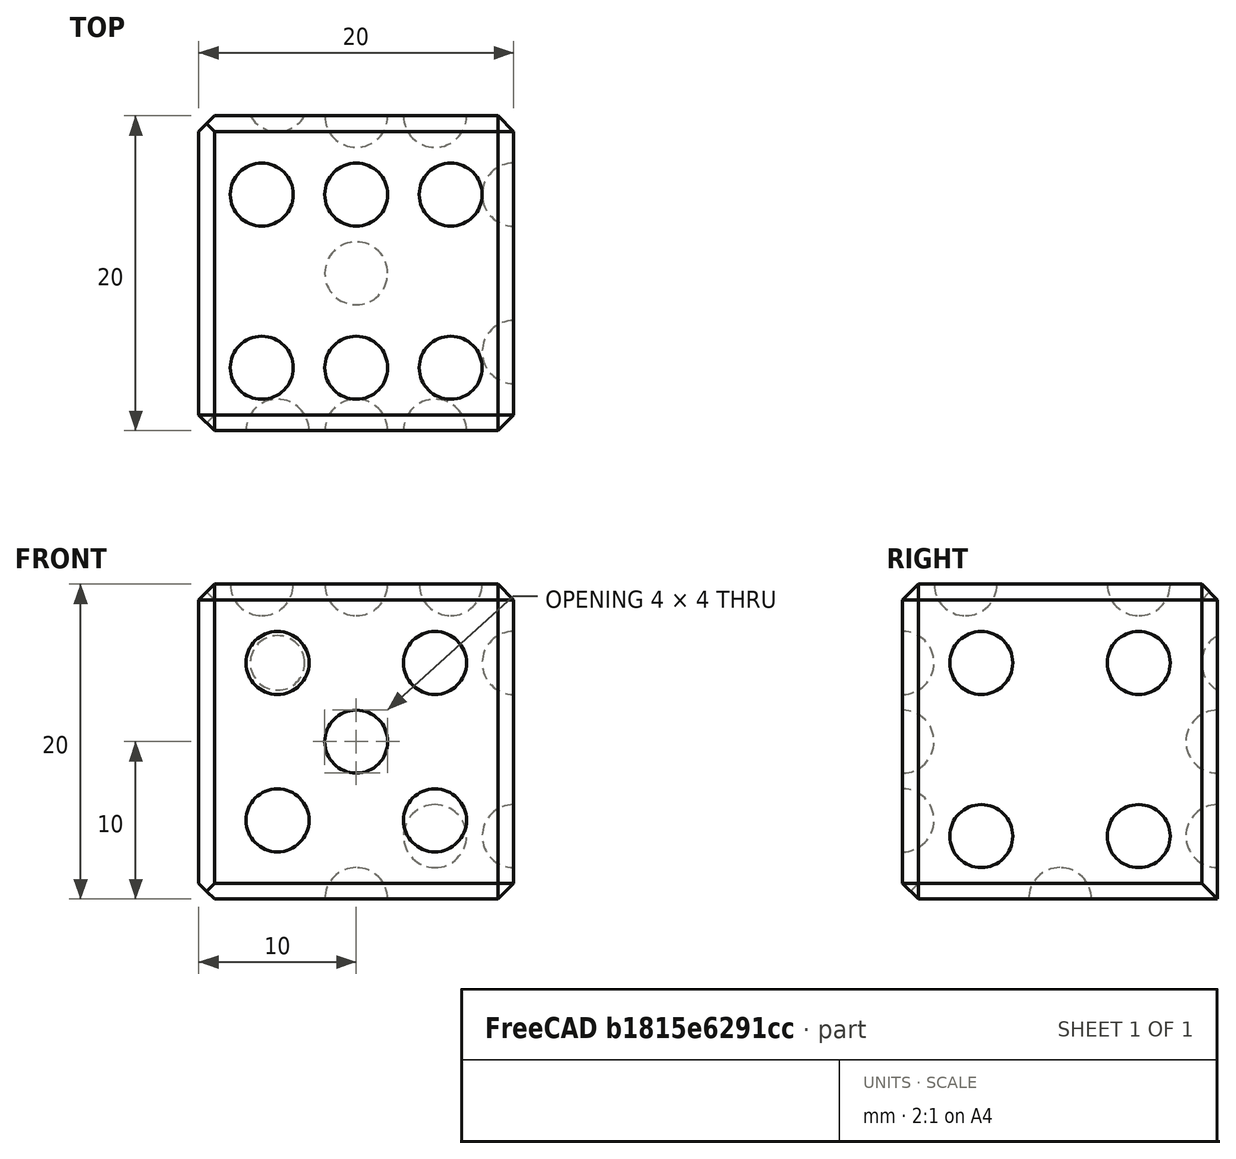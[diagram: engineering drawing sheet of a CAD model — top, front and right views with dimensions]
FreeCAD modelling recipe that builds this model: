
FCSTD DOCUMENT  (FreeCAD 0.21R33694 (Git))
Label: OJT1_T013R012_DAU
License: All rights reserved
LicenseURL: http://en.wikipedia.org/wiki/All_rights_reserved
objects: Part::Sphere×21, Part::MultiFuse×7, Part::Cut×6, Part::Chamfer×3, Part::Box×1
note: 38 computed .brp shape members not serialized (recipe doc carries the construction recipe); baked Part::Feature solids carry a one-line shape summary decoded from their .brp

FEATURE [Part::Box] Box  label="DAU"
  AttacherType = Attacher::AttachEngine3D
  Height = 20
  Length = 20
  Width = 20
FEATURE [Part::Sphere] Sphere
  Angle1 = -90
  Angle2 = 90
  Angle3 = 360
  AttacherType = Attacher::AttachEngine3D
  Placement = pos=(4,4,20) rot=(0,0,1;0rad)
  Radius = 2
FEATURE [Part::Chamfer] Chamfer
  Base = -> Box
  Edges = 9 edges r=1: [Edge1,Edge2,Edge5,Edge6,Edge7,Edge8,Edge9,Edge10,Edge12]
FEATURE [Part::Chamfer] Chamfer001
  Base = -> Chamfer
  Edges = 1 edges r=1: [Edge1]
FEATURE [Part::Chamfer] Chamfer002
  Base = -> Chamfer001
  Edges = 1 edges r=1: [Edge3]
FEATURE [Part::Sphere] Sphere001
  Angle1 = -90
  Angle2 = 90
  Angle3 = 360
  AttacherType = Attacher::AttachEngine3D
  Placement = pos=(10,4,20) rot=(0,0,1;0rad)
  Radius = 2
FEATURE [Part::Sphere] Sphere002
  Angle1 = -90
  Angle2 = 90
  Angle3 = 360
  AttacherType = Attacher::AttachEngine3D
  Placement = pos=(16,4,20) rot=(0,0,1;0rad)
  Radius = 2
FEATURE [Part::MultiFuse] Fusion
  Refine = true
  Shapes = -> [Sphere,Sphere001,Sphere002]
FEATURE [Part::Sphere] Sphere003
  Angle1 = -90
  Angle2 = 90
  Angle3 = 360
  AttacherType = Attacher::AttachEngine3D
  Placement = pos=(4,4,20) rot=(0,0,1;0rad)
  Radius = 2
FEATURE [Part::Sphere] Sphere004
  Angle1 = -90
  Angle2 = 90
  Angle3 = 360
  AttacherType = Attacher::AttachEngine3D
  Placement = pos=(10,4,20) rot=(0,0,1;0rad)
  Radius = 2
FEATURE [Part::Sphere] Sphere005
  Angle1 = -90
  Angle2 = 90
  Angle3 = 360
  AttacherType = Attacher::AttachEngine3D
  Placement = pos=(16,4,20) rot=(0,0,1;0rad)
  Radius = 2
FEATURE [Part::MultiFuse] Fusion001
  Placement = pos=(0,11,0) rot=(0,0,1;0rad)
  Refine = true
  Shapes = -> [Sphere003,Sphere004,Sphere005]
FEATURE [Part::MultiFuse] Fusion002
  Refine = true
  Shapes = -> [Fusion001,Fusion]
FEATURE [Part::Sphere] Sphere006
  Angle1 = -90
  Angle2 = 90
  Angle3 = 360
  AttacherType = Attacher::AttachEngine3D
  Placement = pos=(10,0,10) rot=(0,0,1;0rad)
  Radius = 2
FEATURE [Part::Sphere] Sphere007
  Angle1 = -90
  Angle2 = 90
  Angle3 = 360
  AttacherType = Attacher::AttachEngine3D
  Placement = pos=(15,0,15) rot=(0,0,1;0rad)
  Radius = 2
FEATURE [Part::Sphere] Sphere008
  Angle1 = -90
  Angle2 = 90
  Angle3 = 360
  AttacherType = Attacher::AttachEngine3D
  Placement = pos=(15,0,5) rot=(0,0,1;0rad)
  Radius = 2
FEATURE [Part::Sphere] Sphere009
  Angle1 = -90
  Angle2 = 90
  Angle3 = 360
  AttacherType = Attacher::AttachEngine3D
  Placement = pos=(5,0,5) rot=(0,0,1;0rad)
  Radius = 2
FEATURE [Part::Sphere] Sphere010
  Angle1 = -90
  Angle2 = 90
  Angle3 = 360
  AttacherType = Attacher::AttachEngine3D
  Placement = pos=(5,0,15) rot=(0,0,1;0rad)
  Radius = 2
FEATURE [Part::MultiFuse] Fusion003
  Refine = true
  Shapes = -> [Sphere006,Sphere007,Sphere008,Sphere009,Sphere010]
FEATURE [Part::Sphere] Sphere011
  Angle1 = -90
  Angle2 = 90
  Angle3 = 360
  AttacherType = Attacher::AttachEngine3D
  Placement = pos=(20,5,4) rot=(0,0,1;0rad)
  Radius = 2
FEATURE [Part::Sphere] Sphere012
  Angle1 = -90
  Angle2 = 90
  Angle3 = 360
  AttacherType = Attacher::AttachEngine3D
  Placement = pos=(20,15,4) rot=(0,0,1;0rad)
  Radius = 2
FEATURE [Part::Sphere] Sphere013
  Angle1 = -90
  Angle2 = 90
  Angle3 = 360
  AttacherType = Attacher::AttachEngine3D
  Placement = pos=(20,5,15) rot=(0,0,1;0rad)
  Radius = 2
FEATURE [Part::Sphere] Sphere014
  Angle1 = -90
  Angle2 = 90
  Angle3 = 360
  AttacherType = Attacher::AttachEngine3D
  Placement = pos=(20,15,15) rot=(0,0,1;0rad)
  Radius = 2
FEATURE [Part::MultiFuse] Fusion004
  Refine = true
  Shapes = -> [Sphere011,Sphere012,Sphere013,Sphere014]
FEATURE [Part::Sphere] Sphere015
  Angle1 = -90
  Angle2 = 90
  Angle3 = 360
  AttacherType = Attacher::AttachEngine3D
  Placement = pos=(10,10,0) rot=(0,0,1;0rad)
  Radius = 2
FEATURE [Part::Sphere] Sphere016
  Angle1 = -90
  Angle2 = 90
  Angle3 = 360
  AttacherType = Attacher::AttachEngine3D
  Placement = pos=(0,15,10) rot=(0,0,1;0rad)
  Radius = 2
FEATURE [Part::Sphere] Sphere017
  Angle1 = -90
  Angle2 = 90
  Angle3 = 360
  AttacherType = Attacher::AttachEngine3D
  Placement = pos=(0,5,10) rot=(0,0,1;0rad)
  Radius = 2
FEATURE [Part::MultiFuse] Fusion005
  Refine = true
  Shapes = -> [Sphere016,Sphere017]
FEATURE [Part::Sphere] Sphere018
  Angle1 = -90
  Angle2 = 90
  Angle3 = 360
  AttacherType = Attacher::AttachEngine3D
  Placement = pos=(15,20,4) rot=(0,0,1;0rad)
  Radius = 2
FEATURE [Part::Sphere] Sphere019
  Angle1 = -90
  Angle2 = 90
  Angle3 = 360
  AttacherType = Attacher::AttachEngine3D
  Placement = pos=(10,20,10) rot=(0,0,1;0rad)
  Radius = 2
FEATURE [Part::Sphere] Sphere020
  Angle1 = -90
  Angle2 = 90
  Angle3 = 360
  AttacherType = Attacher::AttachEngine3D
  Placement = pos=(5,21,15) rot=(0,0,1;0rad)
  Radius = 2
FEATURE [Part::MultiFuse] Fusion006
  Refine = true
  Shapes = -> [Sphere020,Sphere019,Sphere018]
FEATURE [Part::Cut] Cut
  Base = -> Chamfer002
  Refine = true
  Tool = -> Fusion006
FEATURE [Part::Cut] Cut001
  Base = -> Chamfer002
  Refine = true
  Tool = -> Fusion005
FEATURE [Part::Cut] Cut002
  Base = -> Chamfer002
  Refine = true
  Tool = -> Sphere015
FEATURE [Part::Cut] Cut003
  Base = -> Chamfer002
  Refine = true
  Tool = -> Fusion004
FEATURE [Part::Cut] Cut004
  Base = -> Chamfer002
  Refine = true
  Tool = -> Fusion003
FEATURE [Part::Cut] Cut005
  Base = -> Chamfer002
  Refine = true
  Tool = -> Fusion002
